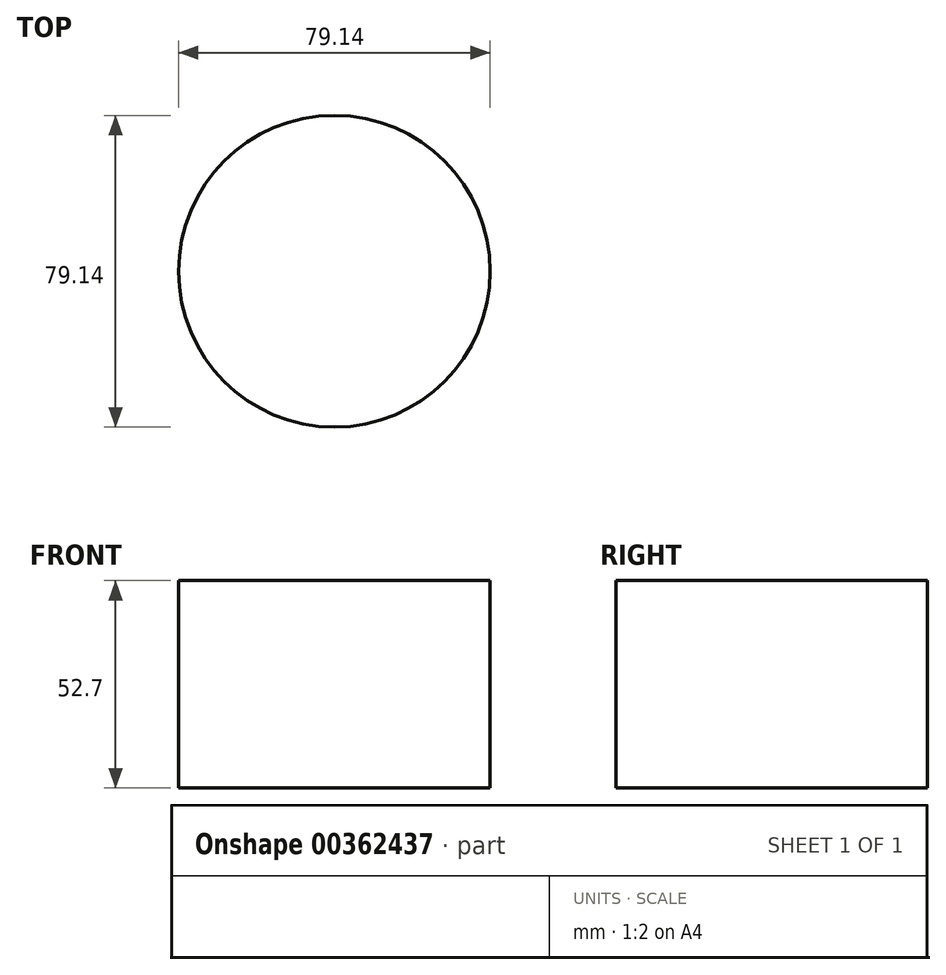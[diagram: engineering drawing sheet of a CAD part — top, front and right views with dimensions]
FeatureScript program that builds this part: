
annotation { "Feature Type Name" : "Feature", "Feature Type Description" : "" }
export const myFeature = defineFeature(function(context is Context, id is Id, definition is map)
    precondition{}
    {
        {
            var Q0;
            Q0=qCreatedBy(makeId("Top.planeOp"),FACE);
            var sketch = newSketch(context, id + "F0", { "sketchPlane" : qUnion([Q0])});
            skCircle(sketch, "E0", {"center": v(0, 0) * mm, "radius": 39.57 * mm});
            skSolve(sketch);
        }
        {
            var Q0;
            Q0=makeQuery(id+"F0.imprint","IMPRINT",FACE,{"disambiguationData":[TD([[makeQuery(id+"F0.imprint","IMPRINT",EDGE,{"derivedFrom":sQuery(id+"F0.wireOp",EDGE,"E0")}),1.0]])]});
            extrude(context, id + "F1", {"entities" : qUnion([Q0]), "depth" : 52.7 * mm});
        }
    });
